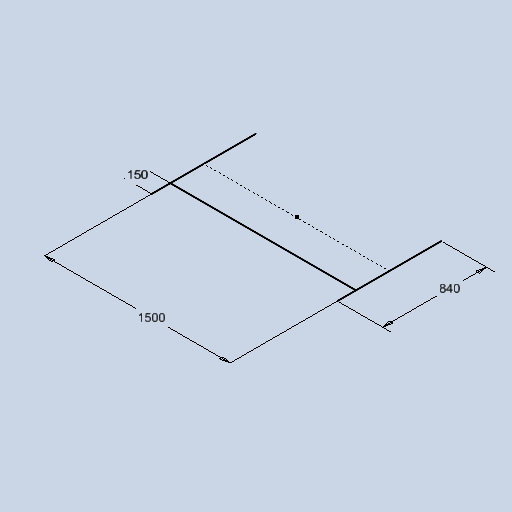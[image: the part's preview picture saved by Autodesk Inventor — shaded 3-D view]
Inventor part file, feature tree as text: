
AUTODESK INVENTOR PART (.ipt)
format: ipt  version: 2025 (Build 290162010, 162A)  size: 128,000 bytes
history: native  units: mm
features: sketch x1
ambient origin geometry x8: Origin, YZ Plane, XZ Plane, XY Plane, X Axis, Y Axis, Z Axis, Center Point
feature tree (1):
  sketch  "Sketch1"  dims[d0=1500.0mm d1=840.0mm d2=150.0mm]
